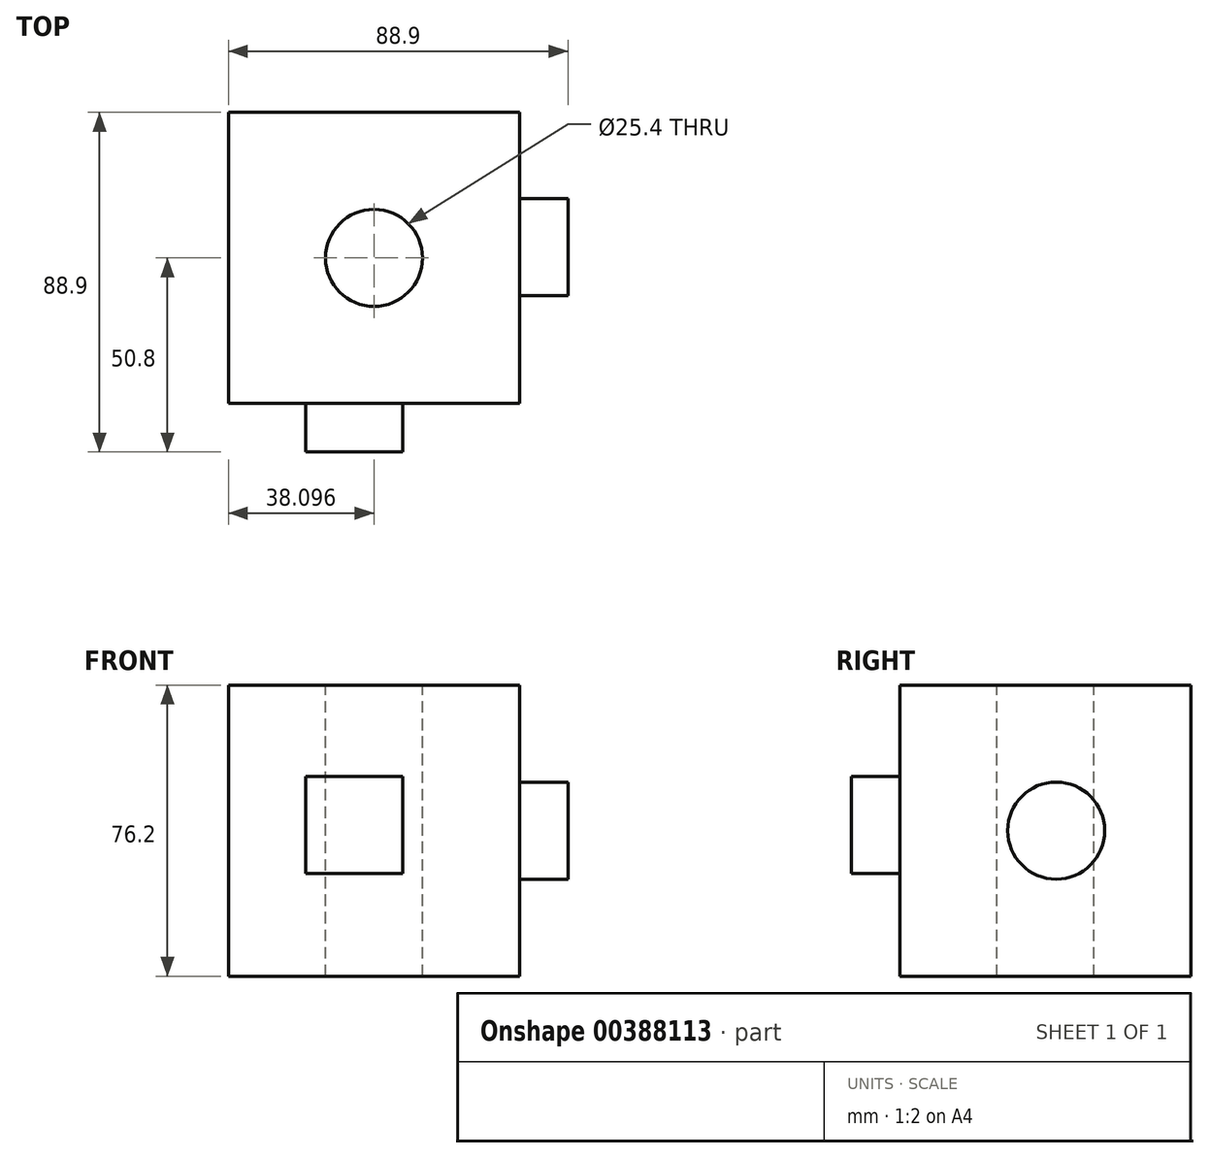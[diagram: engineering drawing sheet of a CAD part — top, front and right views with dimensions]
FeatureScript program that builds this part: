
annotation { "Feature Type Name" : "Feature", "Feature Type Description" : "" }
export const myFeature = defineFeature(function(context is Context, id is Id, definition is map)
    precondition{}
    {
        {
            var Q0;
            Q0=qCreatedBy(makeId("Front.planeOp"),FACE);
            var sketch = newSketch(context, id + "F0", { "sketchPlane" : qUnion([Q0])});
            skLineSegment(sketch, "E0.bottom", {"start": v(-42.42, 49.29) * mm, "end": v(33.78, 49.29) * mm});
            skLineSegment(sketch, "E0.top", {"start": v(-42.42, -26.91) * mm, "end": v(33.78, -26.91) * mm});
            skLineSegment(sketch, "E0.left", {"start": v(-42.42, 49.29) * mm, "end": v(-42.42, -26.91) * mm});
            skLineSegment(sketch, "E0.right", {"start": v(33.78, 49.29) * mm, "end": v(33.78, -26.91) * mm});
            skSolve(sketch);
        }
        {
            var Q0;
            Q0 = qSketchRegion(id + "F0", true);
            extrude(context, id + "F1", {"entities" : qUnion([Q0]), "depth" : 76.2 * mm});
        }
        {
            var Q0;
            Q0=makeQuery(id+"F1.opExtrude","SWEPT_FACE",FACE,{"disambiguationData":[OSD([sQuery(id+"F0.wireOp",EDGE,"E0.bottom")])]});
            var sketch = newSketch(context, id + "F2", { "sketchPlane" : qUnion([Q0])});
            skPoint(sketch, "E1", {"position": v(-4.32, -38.1) * mm});
            skSolve(sketch);
        }
        {
            var Q0;
            Q0=sQuery(id+"F2.wireOp",VERTEX,"E1");
            var Q1;
            Q1=makeQuery(id+"F1.opExtrude","SWEPT_BODY",BODY,{"disambiguationData":[OSD([sQuery(id+"F0.wireOp",EDGE,"E0.bottom"),sQuery(id+"F0.wireOp",EDGE,"E0.top"),sQuery(id+"F0.wireOp",EDGE,"E0.left"),sQuery(id+"F0.wireOp",EDGE,"E0.right")])]});
            hole(context, id + "F3", {"style" : HoleStyle.SIMPLE, "endStyle" : HoleEndStyle.THROUGH, "holeDiameter" : 25.4 * mm, "isTappedThrough" : true, "tappedDepth" : 12.7 * mm, "tapClearance" : 3, "locations" : qUnion([Q0]), "scope" : qUnion([Q1])});
        }
        {
            var Q0;
            Q0=makeQuery(id+"F1.opExtrude","CAP_FACE",FACE,{"disambiguationData":[OSD([sQuery(id+"F0.wireOp",EDGE,"E0.bottom"),sQuery(id+"F0.wireOp",EDGE,"E0.top"),sQuery(id+"F0.wireOp",EDGE,"E0.left"),sQuery(id+"F0.wireOp",EDGE,"E0.right")])],"isStart":false});
            var sketch = newSketch(context, id + "F4", { "sketchPlane" : qUnion([Q0])});
            skLineSegment(sketch, "E2.bottom", {"start": v(-22.21, 25.4) * mm, "end": v(3.19, 25.4) * mm});
            skLineSegment(sketch, "E2.top", {"start": v(-22.21, 0) * mm, "end": v(3.19, 0) * mm});
            skLineSegment(sketch, "E2.left", {"start": v(-22.21, 25.4) * mm, "end": v(-22.21, 0) * mm});
            skLineSegment(sketch, "E2.right", {"start": v(3.19, 25.4) * mm, "end": v(3.19, 0) * mm});
            skSolve(sketch);
        }
        {
            var Q0;
            Q0 = qSketchRegion(id + "F4", true);
            extrude(context, id + "F5", {"entities" : qUnion([Q0]), "operationType" : NewBodyOperationType.ADD, "depth" : 12.7 * mm});
        }
        {
            var Q0;
            Q0=makeQuery(id+"F1.opExtrude","SWEPT_FACE",FACE,{"disambiguationData":[OSD([sQuery(id+"F0.wireOp",EDGE,"E0.right")])]});
            var sketch = newSketch(context, id + "F6", { "sketchPlane" : qUnion([Q0])});
            skCircle(sketch, "E3", {"center": v(-35.27, 11.19) * mm, "radius": 12.7 * mm});
            skSolve(sketch);
        }
        {
            var Q0;
            Q0=makeQuery(id+"F6.imprint","IMPRINT",FACE,{"disambiguationData":[TD([[makeQuery(id+"F6.imprint","IMPRINT",EDGE,{"derivedFrom":sQuery(id+"F6.wireOp",EDGE,"E3")}),1.0]])]});
            extrude(context, id + "F7", {"entities" : qUnion([Q0]), "operationType" : NewBodyOperationType.ADD, "depth" : 12.7 * mm});
        }
    });
